# Revit family: Control_Panels-Lutron-DIN_Rail_Panel_With_Breaker
name_source: partatom
category: Electrical Equipment
revit_build: Autodesk Revit 2017 (Build: 20160225_1515(x64)
units: mm (PartAtom-declared; Revit-internal decimal feet)

## family parameters
Cut with Voids When Loaded = No
Host = Face
OmniClass Number = 23.80.30.11.17
OmniClass Title = Distribution Boards and Control Panels
Panel Configuration = Two Columns, Circuits Across
Part Type = Panelboard
Room Calculation Point = No
Round Connector Dimension = Use Radius
Shared = No

## types (4) — shared parameters
Assembly Code = D5020
Description = DIN Rail Panels
Electrical Connector Distance = 64.5 "
Electrical Potential = 120 V
Feed Through Control Circuit Voltage = 120 V
Finish = Steel - Lutron - Black
Frequency = 60 Hz
Ground Bus = Yes
Instruction Sheet Link = http://www.lutron.com
Load Classification = Power
MCB Rating = 125 A
Manufacturer = Lutron Electronics Co., Inc
Manufacturer Fax Number = 610-282-1243
Neutral Bus = Yes
Neutral Rating = 0.00%
Number of Poles = 1
Overall Depth = 3.94 "
Overall Height = 64.5 "
Overall Width = 15.125 "
Performance URL = http://www.lutron.com
Phase = 1
Power Factor = 1
Product Documentation Link = http://www.lutron.com
Product Name = DIN Rail Panel Enclosure
Product Page URL = http://www.lutron.com
Recessed = Yes
Series = HomeWorks QS
SubFeed Lugs = No
Surface = No
URL = http://www.lutron.com
Unit Weight = 0.00 lb
Version = 2017 - v1.0a
Video Link = https://www.youtube.com
Voltage = 120.00 V
Warranty URL = http://www.lutron.com
zero-valued in all types: Cost, Default Elevation, Offset C

## type names (no varying parameters)
- PD8-65A-120L3-20
- PD8-65A-120L3-15
- PD8-65A-120L4-15
- PD8-65A-120L4-20

note: column(s) folded — value = type name in every type: Model

## geometry (parser evidence)
native form markers: Sweep x2
no freeform markers — native parametric forms only
